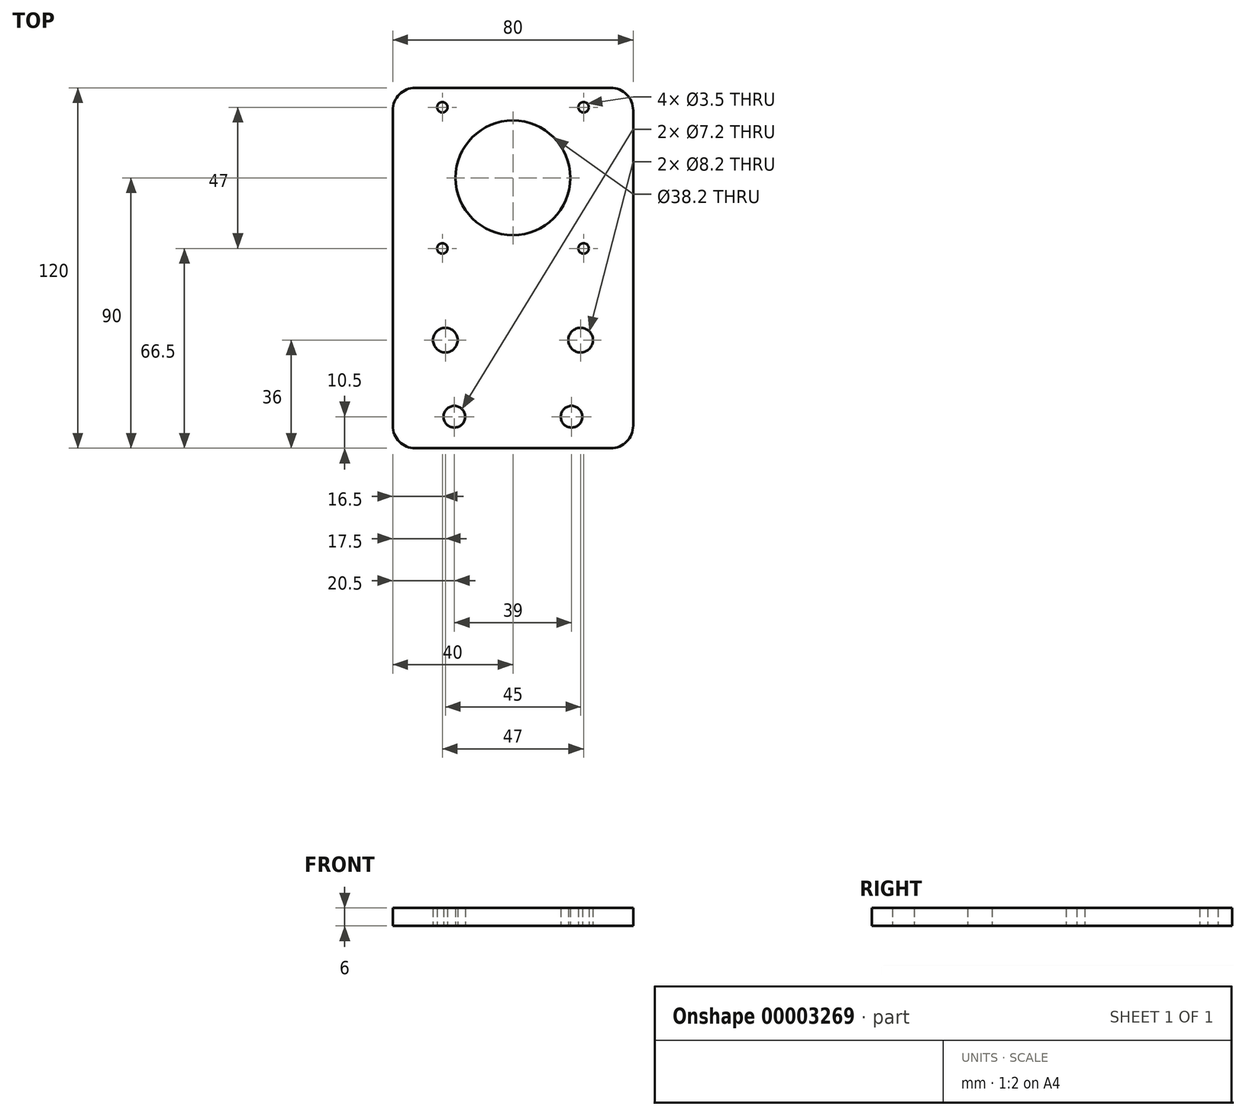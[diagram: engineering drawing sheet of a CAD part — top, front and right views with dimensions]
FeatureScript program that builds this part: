
annotation { "Feature Type Name" : "Feature", "Feature Type Description" : "" }
export const myFeature = defineFeature(function(context is Context, id is Id, definition is map)
    precondition{}
    {
        {
            var Q0;
            Q0=qCreatedBy(makeId("Top.planeOp"),FACE);
            var sketch = newSketch(context, id + "F0", { "sketchPlane" : qUnion([Q0])});
            skLineSegment(sketch, "E0.rect.bottom", {"start": v(-32.5, 60) * mm, "end": v(32.5, 60) * mm});
            skLineSegment(sketch, "E0.rect.top", {"start": v(-32.5, -60) * mm, "end": v(32.5, -60) * mm});
            skLineSegment(sketch, "E0.rect.left", {"start": v(-40, 52.5) * mm, "end": v(-40, -52.5) * mm});
            skLineSegment(sketch, "E0.rect.right", {"start": v(40, 52.5) * mm, "end": v(40, -52.5) * mm});
            skPoint(sketch, "E0.rect.middle", {"position": v(0, 0) * mm});
            skLineSegment(sketch, "E1", {"start": v(0, 0) * mm, "end": v(0, 87.7) * mm, "construction": true});
            skCircle(sketch, "E2", {"center": v(0, 30) * mm, "radius": 19.1 * mm});
            skLineSegment(sketch, "E3", {"start": v(-51.35, -49.5) * mm, "end": v(61.53, -49.5) * mm, "construction": true});
            skCircle(sketch, "E4", {"center": v(-23.5, 53.5) * mm, "radius": 1.75 * mm});
            skCircle(sketch, "E5", {"center": v(-23.5, 6.5) * mm, "radius": 1.75 * mm});
            skCircle(sketch, "E6", {"center": v(23.5, 6.5) * mm, "radius": 1.75 * mm});
            skCircle(sketch, "E7", {"center": v(23.5, 53.5) * mm, "radius": 1.75 * mm});
            skCircle(sketch, "E8", {"center": v(-19.5, -49.5) * mm, "radius": 3.6 * mm});
            skCircle(sketch, "E9", {"center": v(19.5, -49.5) * mm, "radius": 3.6 * mm});
            skCircle(sketch, "E10", {"center": v(-22.5, -24) * mm, "radius": 4.1 * mm});
            skCircle(sketch, "E11", {"center": v(22.5, -24) * mm, "radius": 4.1 * mm});
            skLineSegment(sketch, "E12", {"start": v(-46.68, 30) * mm, "end": v(46.68, 30) * mm, "construction": true});
            skLineSegment(sketch, "E13", {"start": v(-47, -24) * mm, "end": v(46.05, -24) * mm, "construction": true});
            skPoint(sketch, "E14.visualSharp", {"position": v(40, 60) * mm});
            skArc(sketch, "E14.filletArc", {"start": v(40, 52.5) * mm, "mid": v(37.8, 57.8) * mm, "end": v(32.5, 60) * mm});
            skPoint(sketch, "E15.visualSharp", {"position": v(-40, 60) * mm});
            skArc(sketch, "E15.filletArc", {"start": v(-32.5, 60) * mm, "mid": v(-37.8, 57.8) * mm, "end": v(-40, 52.5) * mm});
            skPoint(sketch, "E16.visualSharp", {"position": v(40, -60) * mm});
            skArc(sketch, "E16.filletArc", {"start": v(32.5, -60) * mm, "mid": v(37.8, -57.8) * mm, "end": v(40, -52.5) * mm});
            skPoint(sketch, "E17.visualSharp", {"position": v(-40, -60) * mm});
            skArc(sketch, "E17.filletArc", {"start": v(-40, -52.5) * mm, "mid": v(-37.8, -57.8) * mm, "end": v(-32.5, -60) * mm});
            skCircle(sketch, "E18", {"center": v(-19.5, -49.5) * mm, "radius": 16 * mm, "construction": true});
            skCircle(sketch, "E19", {"center": v(19.5, -49.5) * mm, "radius": 16 * mm, "construction": true});
            skLineSegment(sketch, "E20", {"start": v(-18.99, -65.5) * mm, "end": v(44.24, -65.5) * mm, "construction": true});
            skSolve(sketch);
        }
        {
            var Q0;
            Q0=makeQuery(id+"F0.imprint","IMPRINT",FACE,{"disambiguationData":[TD([[makeQuery(id+"F0.imprint","IMPRINT",EDGE,{"derivedFrom":sQuery(id+"F0.wireOp",EDGE,"E0.rect.bottom")}),-1.0]])]});
            extrude(context, id + "F1", {"entities" : qUnion([Q0]), "depth" : 6 * mm});
        }
    });
